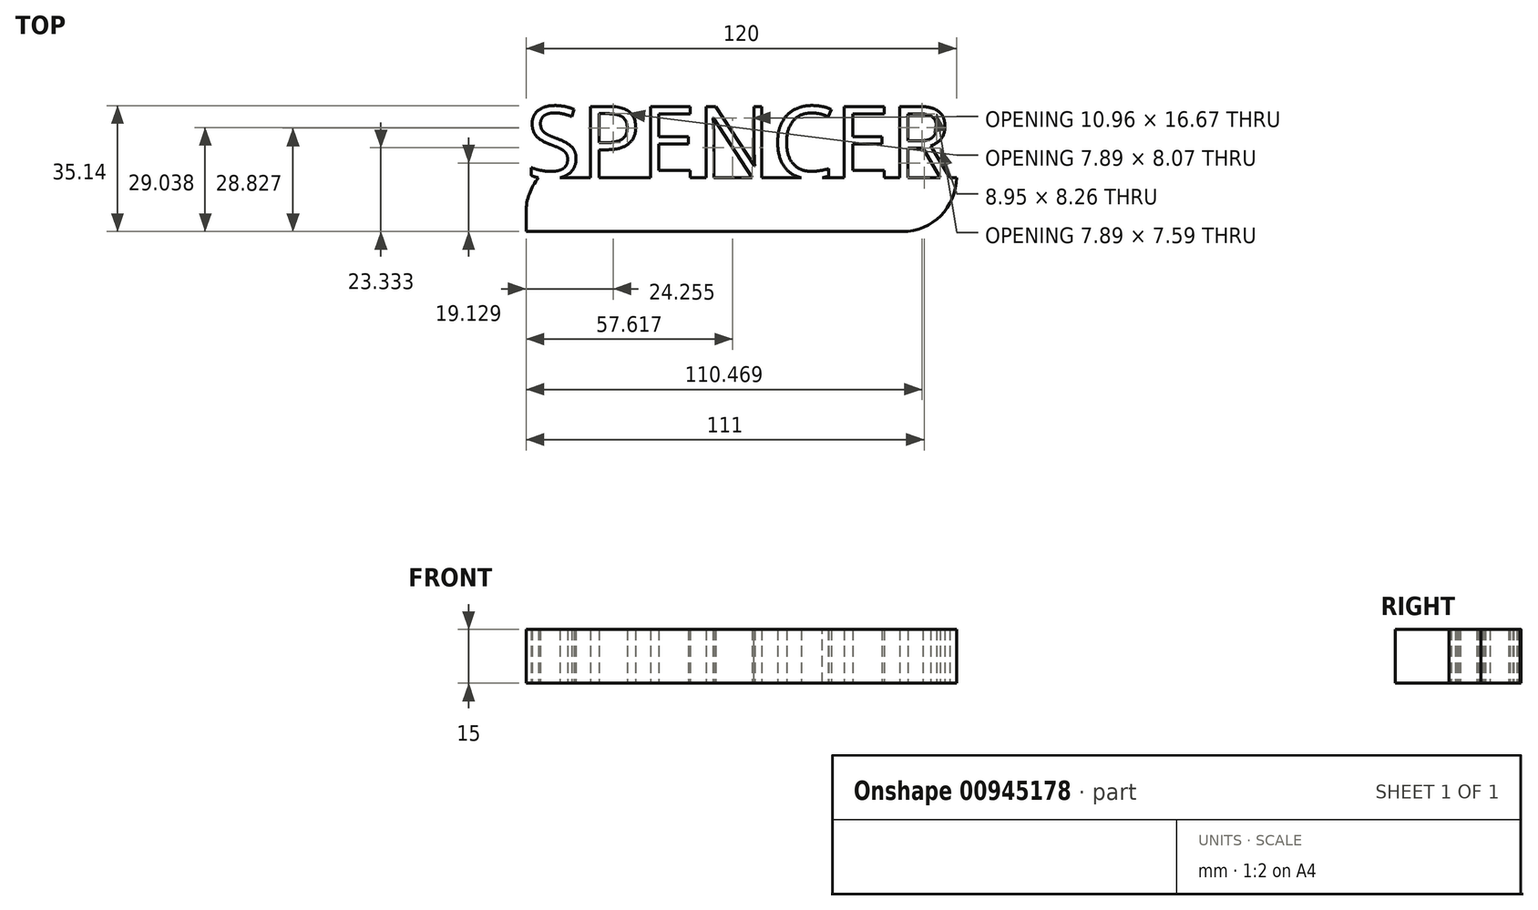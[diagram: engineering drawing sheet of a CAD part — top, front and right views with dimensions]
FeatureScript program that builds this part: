
annotation { "Feature Type Name" : "Feature", "Feature Type Description" : "" }
export const myFeature = defineFeature(function(context is Context, id is Id, definition is map)
    precondition{}
    {
        {
            var Q0;
            Q0=qCreatedBy(makeId("Top.planeOp"),FACE);
            var sketch = newSketch(context, id + "F0", { "sketchPlane" : qUnion([Q0])});
            skLineSegment(sketch, "E0.bottom", {"start": v(0, 0) * mm, "end": v(-120, 0) * mm});
            skLineSegment(sketch, "E0.top", {"start": v(0, 15) * mm, "end": v(-120, 15) * mm});
            skLineSegment(sketch, "E0.left", {"start": v(0, 0) * mm, "end": v(0, 15) * mm});
            skLineSegment(sketch, "E0.right", {"start": v(-120, 0) * mm, "end": v(-120, 15) * mm});
            skText(sketch, "E1", { "text": "SPENCER", "fontName": "OpenSans-Regular.ttf"});
            const initialGuessF0  = {"E1": [-0.12, 0.015, 1, 0, 0.02003]};
            skSetInitialGuess(sketch, initialGuessF0);
            skSolve(sketch);
        }
        {
            var Q0;
            Q0 = qSketchRegion(id + "F0", true);
            extrude(context, id + "F1", {"entities" : qUnion([Q0]), "depth" : 15 * mm, "offsetDistance" : 25 * mm});
        }
        {
            var Q0;
            Q0=makeQuery(id+"F1.opExtrude","SWEPT_EDGE",EDGE,{"disambiguationData":[OSD([sQuery(id+"F0.wireOp",EDGE,"E0.top"),sQuery(id+"F0.wireOp",EDGE,"E0.right")])]});
            var Q1;
            Q1=makeQuery(id+"F1.opExtrude","SWEPT_EDGE",EDGE,{"disambiguationData":[OSD([sQuery(id+"F0.wireOp",EDGE,"E0.bottom"),sQuery(id+"F0.wireOp",EDGE,"E0.left")])]});
            fillet(context, id + "F2", {"entities" : qUnion([Q0, Q1]), "radius" : 15 * mm, "tangentPropagation" : true, "allowEdgeOverflow" : false});
        }
    });
